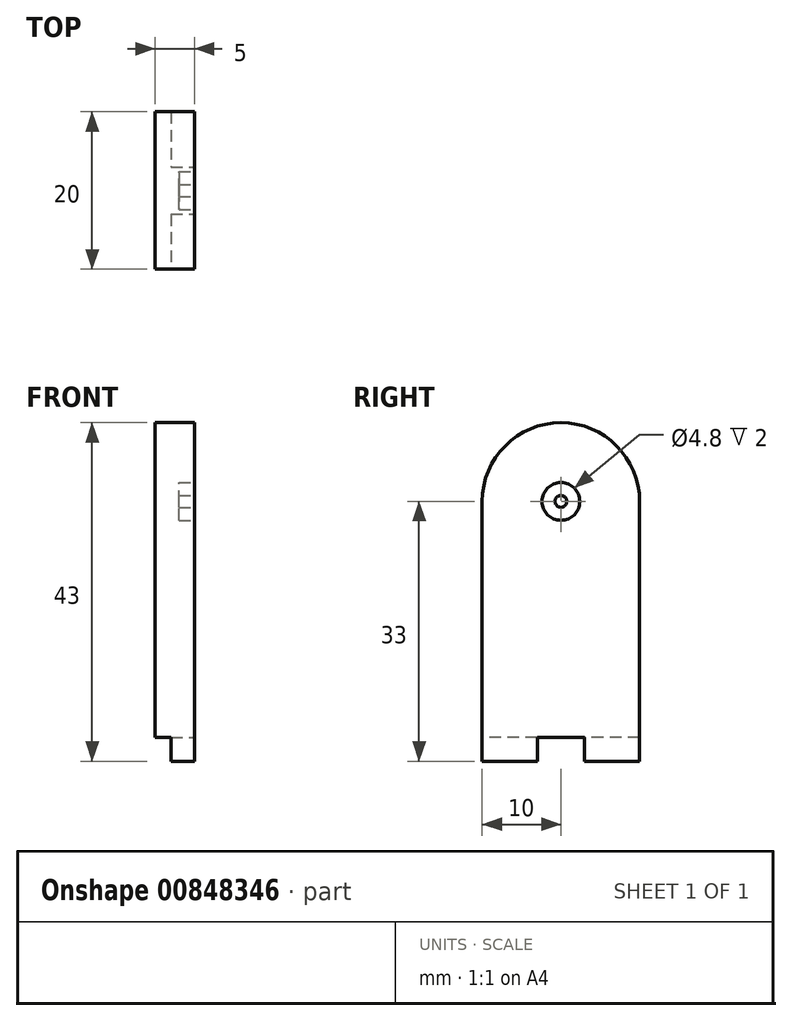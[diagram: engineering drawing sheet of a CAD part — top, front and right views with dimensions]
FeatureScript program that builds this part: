
annotation { "Feature Type Name" : "Feature", "Feature Type Description" : "" }
export const myFeature = defineFeature(function(context is Context, id is Id, definition is map)
    precondition{}
    {
        {
            var Q0;
            Q0=qCreatedBy(makeId("Right.planeOp"),FACE);
            var sketch = newSketch(context, id + "F0", { "sketchPlane" : qUnion([Q0])});
            skArc(sketch, "E0", {"start": v(-10, 30) * mm, "mid": v(0, 40) * mm, "end": v(10, 30) * mm});
            skLineSegment(sketch, "E1", {"start": v(-10, 0) * mm, "end": v(-10, 30) * mm});
            skLineSegment(sketch, "E2", {"start": v(10, 30) * mm, "end": v(10, 0) * mm});
            skLineSegment(sketch, "E3", {"start": v(10, 0) * mm, "end": v(-10, 0) * mm});
            skSolve(sketch);
        }
        {
            var Q0;
            Q0 = qSketchRegion(id + "F0", true);
            extrude(context, id + "F1", {"entities" : qUnion([Q0]), "depth" : 5 * mm, "offsetDistance" : 25 * mm});
        }
        {
            var Q0;
            Q0=makeQuery(id+"F1.opExtrude","CAP_FACE",FACE,{"disambiguationData":[OSD([sQuery(id+"F0.wireOp",EDGE,"E0"),sQuery(id+"F0.wireOp",EDGE,"E1"),sQuery(id+"F0.wireOp",EDGE,"E2"),sQuery(id+"F0.wireOp",EDGE,"E3")])],"isStart":false});
            var sketch = newSketch(context, id + "F2", { "sketchPlane" : qUnion([Q0])});
            skCircle(sketch, "E4", {"center": v(0, 30) * mm, "radius": 2.4 * mm});
            skCircle(sketch, "E5", {"center": v(0, 30) * mm, "radius": 0.75 * mm});
            skSolve(sketch);
        }
        {
            var Q0;
            Q0 = qSketchRegion(id + "F2", true);
            extrude(context, id + "F3", {"entities" : qUnion([Q0]), "operationType" : NewBodyOperationType.REMOVE, "oppositeDirection" : true, "depth" : 2 * mm, "offsetDistance" : 25 * mm});
        }
        {
            var Q0;
            {var subQ0=sQuery(id+"F0.wireOp",EDGE,"E2");var subQ1=sQuery(id+"F0.wireOp",EDGE,"E1");var subQ2=sQuery(id+"F0.wireOp",EDGE,"E3");var subQ3=sQuery(id+"F0.wireOp",EDGE,"E0");Q0=makeQuery(id+"F3.boolean.opBoolean","SPLIT",FACE,{"disambiguationData":[TD([makeQuery(id+"F1.opExtrude","SWEPT_FACE",FACE,{"disambiguationData":[OSD([subQ3])]})])],"derivedFrom":makeQuery(id+"F1.opExtrude","CAP_FACE",FACE,{"disambiguationData":[OSD([subQ3,subQ1,subQ0,subQ2])],"isStart":false})});}
            var sketch = newSketch(context, id + "F4", { "sketchPlane" : qUnion([Q0])});
            skLineSegment(sketch, "E6.bottom", {"start": v(-10, 0) * mm, "end": v(-3, 0) * mm});
            skLineSegment(sketch, "E6.top", {"start": v(-10, -3) * mm, "end": v(-3, -3) * mm});
            skLineSegment(sketch, "E6.left", {"start": v(-10, 0) * mm, "end": v(-10, -3) * mm});
            skLineSegment(sketch, "E6.right", {"start": v(-3, 0) * mm, "end": v(-3, -3) * mm});
            skLineSegment(sketch, "E7.bottom", {"start": v(10, 0) * mm, "end": v(3, 0) * mm});
            skLineSegment(sketch, "E7.top", {"start": v(10, -3) * mm, "end": v(3, -3) * mm});
            skLineSegment(sketch, "E7.left", {"start": v(10, 0) * mm, "end": v(10, -3) * mm});
            skLineSegment(sketch, "E7.right", {"start": v(3, 0) * mm, "end": v(3, -3) * mm});
            skSolve(sketch);
        }
        {
            var Q0;
            Q0 = qSketchRegion(id + "F4", true);
            extrude(context, id + "F5", {"entities" : qUnion([Q0]), "operationType" : NewBodyOperationType.ADD, "oppositeDirection" : true, "depth" : 3 * mm, "offsetDistance" : 25 * mm});
        }
    });
